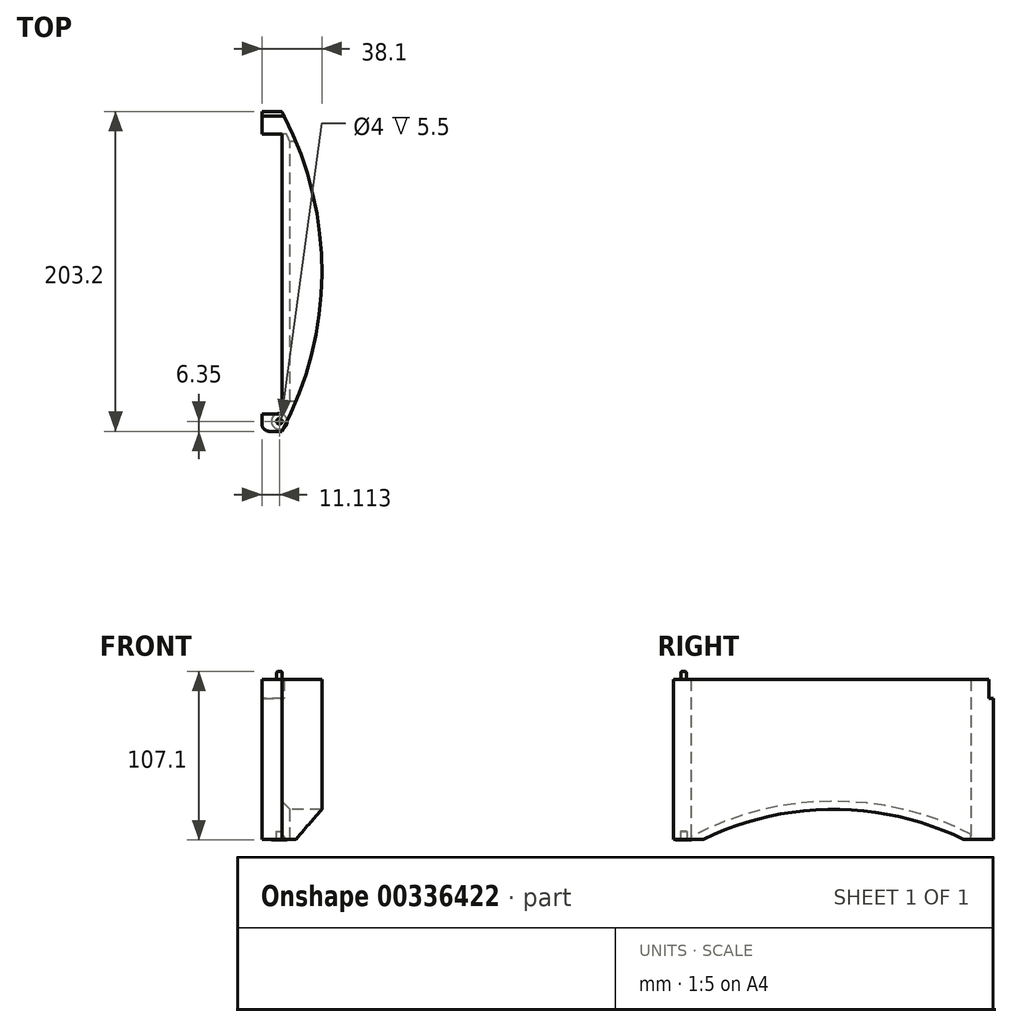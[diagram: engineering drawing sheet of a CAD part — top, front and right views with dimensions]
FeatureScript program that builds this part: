
annotation { "Feature Type Name" : "Feature", "Feature Type Description" : "" }
export const myFeature = defineFeature(function(context is Context, id is Id, definition is map)
    precondition{}
    {
        {
            var Q0;
            Q0=qCreatedBy(makeId("Right.planeOp"),FACE);
            var sketch = newSketch(context, id + "F0", { "sketchPlane" : qUnion([Q0])});
            skLineSegment(sketch, "E0", {"start": v(0, 0) * mm, "end": v(52.75, 0) * mm});
            skLineSegment(sketch, "E1", {"start": v(101.6, 0) * mm, "end": v(101.6, 166.73) * mm, "construction": true});
            skPoint(sketch, "E1.startSnap0", {"position": v(101.6, 30.6) * mm});
            skLineSegment(sketch, "E2", {"start": v(0, 0) * mm, "end": v(0, 101.6) * mm});
            skLineSegment(sketch, "E3", {"start": v(0, 101.6) * mm, "end": v(101.6, 101.6) * mm});
            skLineSegment(sketch, "E4", {"start": v(52.75, 0) * mm, "end": v(101.6, 0) * mm});
            skLineSegment(sketch, "E5.MirrorCS", {"start": v(203.2, 0) * mm, "end": v(203.2, 101.6) * mm});
            skLineSegment(sketch, "E6.MirrorCS", {"start": v(150.45, 0) * mm, "end": v(101.6, 0) * mm});
            skLineSegment(sketch, "E7.MirrorCS", {"start": v(203.2, 101.6) * mm, "end": v(101.6, 101.6) * mm});
            skLineSegment(sketch, "E8.MirrorCS", {"start": v(203.2, 0) * mm, "end": v(150.45, 0) * mm});
            skSolve(sketch);
        }
        {
            var Q0;
            Q0 = qSketchRegion(id + "F0", true);
            extrude(context, id + "F1", {"entities" : qUnion([Q0]), "depth" : 12.7 * mm});
        }
        {
            var Q0;
            Q0=makeQuery(id+"F1.opExtrude","SWEPT_FACE",FACE,{"disambiguationData":[OSD([sQuery(id+"F0.wireOp",EDGE,"E0"),sQuery(id+"F0.wireOp",EDGE,"E4"),sQuery(id+"F0.wireOp",EDGE,"E6.MirrorCS"),sQuery(id+"F0.wireOp",EDGE,"E8.MirrorCS")])]});
            var sketch = newSketch(context, id + "F2", { "sketchPlane" : qUnion([Q0])});
            skArc(sketch, "E9", {"start": v(12.7, -203.2) * mm, "mid": v(38.1, -101.6) * mm, "end": v(12.7, 0) * mm});
            skLineSegment(sketch, "E10", {"start": v(12.7, 0) * mm, "end": v(12.7, -203.2) * mm});
            skSolve(sketch);
        }
        {
            var Q0;
            Q0 = qSketchRegion(id + "F2", true);
            var Q1;
            Q1=makeQuery(id+"F1.opExtrude","SWEPT_FACE",FACE,{"disambiguationData":[OSD([sQuery(id+"F0.wireOp",EDGE,"E3"),sQuery(id+"F0.wireOp",EDGE,"E7.MirrorCS")])]});
            extrude(context, id + "F3", {"entities" : qUnion([Q0]), "operationType" : NewBodyOperationType.ADD, "endBound" : BoundingType.UP_TO_SURFACE, "oppositeDirection" : true, "endBoundEntityFace" : qUnion([Q1]), "depth" : 25 * mm});
        }
        {
            var Q0;
            Q0=makeQuery(id+"F1.opExtrude","CAP_FACE",FACE,{"disambiguationData":[OSD([sQuery(id+"F0.wireOp",EDGE,"E0"),sQuery(id+"F0.wireOp",EDGE,"E2"),sQuery(id+"F0.wireOp",EDGE,"E3"),sQuery(id+"F0.wireOp",EDGE,"E4"),sQuery(id+"F0.wireOp",EDGE,"E5.MirrorCS"),sQuery(id+"F0.wireOp",EDGE,"E6.MirrorCS"),sQuery(id+"F0.wireOp",EDGE,"E7.MirrorCS"),sQuery(id+"F0.wireOp",EDGE,"E8.MirrorCS")])],"isStart":true});
            var sketch = newSketch(context, id + "F4", { "sketchPlane" : qUnion([Q0])});
            skArc(sketch, "E11", {"start": v(-19.05, 0) * mm, "mid": v(-101.6, 19.05) * mm, "end": v(-184.15, 0) * mm});
            skLineSegment(sketch, "E12", {"start": v(-184.15, 0) * mm, "end": v(-19.05, 0) * mm});
            skLineSegment(sketch, "E13", {"start": v(-101.6, 0) * mm, "end": v(-101.6, 101.6) * mm});
            skSolve(sketch);
        }
        {
            var Q0;
            Q0 = qSketchRegion(id + "F4", true);
            extrude(context, id + "F5", {"entities" : qUnion([Q0]), "operationType" : NewBodyOperationType.REMOVE, "endBound" : BoundingType.THROUGH_ALL, "oppositeDirection" : true, "depth" : 25 * mm});
        }
        {
            var Q0;
            Q0=makeQuery(id+"F1.opExtrude","CAP_FACE",FACE,{"disambiguationData":[OSD([sQuery(id+"F0.wireOp",EDGE,"E0"),sQuery(id+"F0.wireOp",EDGE,"E2"),sQuery(id+"F0.wireOp",EDGE,"E3"),sQuery(id+"F0.wireOp",EDGE,"E4"),sQuery(id+"F0.wireOp",EDGE,"E5.MirrorCS"),sQuery(id+"F0.wireOp",EDGE,"E6.MirrorCS"),sQuery(id+"F0.wireOp",EDGE,"E7.MirrorCS"),sQuery(id+"F0.wireOp",EDGE,"E8.MirrorCS")])],"isStart":true});
            var sketch = newSketch(context, id + "F6", { "sketchPlane" : qUnion([Q0])});
            skLineSegment(sketch, "E14.bottom", {"start": v(-242.75, 138.92) * mm, "end": v(-200.2, 138.92) * mm});
            skLineSegment(sketch, "E14.top", {"start": v(-242.75, 89.43) * mm, "end": v(-200.2, 89.43) * mm});
            skLineSegment(sketch, "E14.left", {"start": v(-242.75, 138.92) * mm, "end": v(-242.75, 89.43) * mm});
            skLineSegment(sketch, "E14.right", {"start": v(-200.2, 138.92) * mm, "end": v(-200.2, 89.43) * mm});
            skSolve(sketch);
        }
        {
            var Q0;
            Q0 = qSketchRegion(id + "F6", true);
            extrude(context, id + "F7", {"entities" : qUnion([Q0]), "operationType" : NewBodyOperationType.REMOVE, "endBound" : BoundingType.THROUGH_ALL, "oppositeDirection" : true, "depth" : 25 * mm});
        }
        {
            var Q0;
            {var subQ0=sQuery(id+"F0.wireOp",EDGE,"E8.MirrorCS");var subQ1=sQuery(id+"F0.wireOp",EDGE,"E6.MirrorCS");var subQ2=sQuery(id+"F0.wireOp",EDGE,"E4");var subQ3=sQuery(id+"F0.wireOp",EDGE,"E2");var subQ4=sQuery(id+"F0.wireOp",EDGE,"E0");var subQ5=sQuery(id+"F2.wireOp",EDGE,"E9");Q0=makeQuery(id+"F5.boolean.opBoolean","SPLIT",FACE,{"disambiguationData":[TD([makeQuery(id+"F1.opExtrude","SWEPT_FACE",FACE,{"disambiguationData":[OSD([subQ3])]})])],"derivedFrom":makeQuery(id+"F3.boolean.opBoolean","MERGE",FACE,{"derivedFrom":[makeQuery(id+"F1.opExtrude","SWEPT_FACE",FACE,{"disambiguationData":[OSD([subQ4,subQ2,subQ1,subQ0])]}),makeQuery(id+"F3.opExtrude","CAP_FACE",FACE,{"disambiguationData":[OSD([subQ5,sQuery(id+"F2.wireOp",EDGE,"E10")])],"isStart":true})]})});}
            var sketch = newSketch(context, id + "F8", { "sketchPlane" : qUnion([Q0])});
            skCircle(sketch, "E15", {"center": v(11.11, -6.35) * mm, "radius": 2 * mm});
            skSolve(sketch);
        }
        {
            var Q0;
            Q0 = qSketchRegion(id + "F8", true);
            extrude(context, id + "F9", {"entities" : qUnion([Q0]), "operationType" : NewBodyOperationType.REMOVE, "oppositeDirection" : true, "depth" : 5 * mm});
        }
        {
            var Q0;
            {var subQ0=sQuery(id+"F0.wireOp",EDGE,"E8.MirrorCS");var subQ1=sQuery(id+"F0.wireOp",EDGE,"E6.MirrorCS");var subQ2=sQuery(id+"F0.wireOp",EDGE,"E4");var subQ3=sQuery(id+"F0.wireOp",EDGE,"E2");var subQ4=sQuery(id+"F0.wireOp",EDGE,"E0");var subQ5=sQuery(id+"F2.wireOp",EDGE,"E9");Q0=makeQuery(id+"F5.boolean.opBoolean","SPLIT",FACE,{"disambiguationData":[TD([makeQuery(id+"F1.opExtrude","SWEPT_FACE",FACE,{"disambiguationData":[OSD([subQ3])]})])],"derivedFrom":makeQuery(id+"F3.boolean.opBoolean","MERGE",FACE,{"derivedFrom":[makeQuery(id+"F1.opExtrude","SWEPT_FACE",FACE,{"disambiguationData":[OSD([subQ4,subQ2,subQ1,subQ0])]}),makeQuery(id+"F3.opExtrude","CAP_FACE",FACE,{"disambiguationData":[OSD([subQ5,sQuery(id+"F2.wireOp",EDGE,"E10")])],"isStart":true})]})});}
            var sketch = newSketch(context, id + "F10", { "sketchPlane" : qUnion([Q0])});
            skCircle(sketch, "E16", {"center": v(11.11, -6.35) * mm, "radius": 5 * mm});
            skCircle(sketch, "E17.0", {"center": v(11.11, -6.35) * mm, "radius": 2 * mm});
            skSolve(sketch);
        }
        {
            var Q0;
            Q0 = qSketchRegion(id + "F10", true);
            extrude(context, id + "F11", {"entities" : qUnion([Q0]), "operationType" : NewBodyOperationType.ADD, "depth" : .5 * mm});
        }
        {
            var Q0;
            {var subQ0=sQuery(id+"F0.wireOp",EDGE,"E7.MirrorCS");var subQ1=sQuery(id+"F0.wireOp",EDGE,"E3");Q0=makeQuery(id+"F3.boolean.opBoolean","MERGE",FACE,{"derivedFrom":[makeQuery(id+"F1.opExtrude","SWEPT_FACE",FACE,{"disambiguationData":[OSD([subQ1,subQ0])]}),makeQuery(id+"F3.opExtrude","CAP_FACE",FACE,{"disambiguationData":[OSD([subQ1,subQ0])],"isStart":false})]});}
            var sketch = newSketch(context, id + "F12", { "sketchPlane" : qUnion([Q0])});
            skCircle(sketch, "E18.0", {"center": v(11.11, 6.35) * mm, "radius": 2 * mm, "construction": true});
            skCircle(sketch, "E19.0", {"center": v(11.11, 6.35) * mm, "radius": 1.8 * mm});
            skSolve(sketch);
        }
        {
            var Q0;
            Q0 = qSketchRegion(id + "F12", true);
            extrude(context, id + "F13", {"entities" : qUnion([Q0]), "operationType" : NewBodyOperationType.ADD, "depth" : 5 * mm});
        }
        {
            var Q0;
            Q0=makeQuery(id+"F13.opExtrude","CAP_EDGE",EDGE,{"disambiguationData":[OSD([sQuery(id+"F12.wireOp",EDGE,"E19.0")])],"isStart":false});
            fillet(context, id + "F14", {"entities" : qUnion([Q0]), "radius" : 1 * mm, "tangentPropagation" : true, "allowEdgeOverflow" : false});
        }
        {
            var Q0;
            Q0=makeQuery(id+"F1.opExtrude","CAP_FACE",FACE,{"disambiguationData":[OSD([sQuery(id+"F0.wireOp",EDGE,"E0"),sQuery(id+"F0.wireOp",EDGE,"E2"),sQuery(id+"F0.wireOp",EDGE,"E3"),sQuery(id+"F0.wireOp",EDGE,"E4"),sQuery(id+"F0.wireOp",EDGE,"E5.MirrorCS"),sQuery(id+"F0.wireOp",EDGE,"E6.MirrorCS"),sQuery(id+"F0.wireOp",EDGE,"E7.MirrorCS"),sQuery(id+"F0.wireOp",EDGE,"E8.MirrorCS")])],"isStart":true});
            var sketch = newSketch(context, id + "F15", { "sketchPlane" : qUnion([Q0])});
            skLineSegment(sketch, "E20", {"start": v(-100.1, 101.6) * mm, "end": v(-100.1, 0) * mm, "construction": true});
            skLineSegment(sketch, "E21", {"start": v(-189, 101.6) * mm, "end": v(-189, 0) * mm});
            skLineSegment(sketch, "E22", {"start": v(-189, 0) * mm, "end": v(-100.1, 0) * mm});
            skLineSegment(sketch, "E23", {"start": v(-189, 101.6) * mm, "end": v(-100.1, 101.6) * mm});
            skLineSegment(sketch, "E24.MirrorCS", {"start": v(-11.2, 101.6) * mm, "end": v(-100.1, 101.6) * mm});
            skLineSegment(sketch, "E25.MirrorCS", {"start": v(-11.2, 101.6) * mm, "end": v(-11.2, 0) * mm});
            skLineSegment(sketch, "E26.MirrorCS", {"start": v(-11.2, 0) * mm, "end": v(-100.1, 0) * mm});
            skSolve(sketch);
        }
        {
            var Q0;
            Q0 = qSketchRegion(id + "F15", true);
            extrude(context, id + "F16", {"entities" : qUnion([Q0]), "operationType" : NewBodyOperationType.REMOVE, "oppositeDirection" : true, "depth" : 12.7 * mm});
        }
        {
            var Q0;
            Q0=makeQuery(id+"F1.opExtrude","CAP_EDGE",EDGE,{"disambiguationData":[OSD([sQuery(id+"F0.wireOp",EDGE,"E2")])],"isStart":true});
            var Q1;
            Q1=makeQuery(id+"F16.boolean.opBoolean","COPY",EDGE,{"derivedFrom":makeQuery(id+"F16.opExtrude","CAP_EDGE",EDGE,{"disambiguationData":[OSD([sQuery(id+"F15.wireOp",EDGE,"E25.MirrorCS")])],"isStart":true})});
            fillet(context, id + "F17", {"entities" : qUnion([Q0, Q1]), "radius" : 5.08 * mm, "tangentPropagation" : true, "allowEdgeOverflow" : false});
        }
        {
            var Q0;
            Q0=makeQuery(id+"F16.boolean.opBoolean","INTERSECT",EDGE,{"derivedFrom":[makeQuery(id+"F5.boolean.opBoolean","COPY",FACE,{"derivedFrom":makeQuery(id+"F5.opExtrude","SWEPT_FACE",FACE,{"disambiguationData":[OSD([sQuery(id+"F4.wireOp",EDGE,"E11")])]})}),makeQuery(id+"F16.opExtrude","CAP_FACE",FACE,{"disambiguationData":[OSD([sQuery(id+"F15.wireOp",EDGE,"E21"),sQuery(id+"F15.wireOp",EDGE,"E22"),sQuery(id+"F15.wireOp",EDGE,"E23"),sQuery(id+"F15.wireOp",EDGE,"E24.MirrorCS"),sQuery(id+"F15.wireOp",EDGE,"E25.MirrorCS"),sQuery(id+"F15.wireOp",EDGE,"E26.MirrorCS")])],"isStart":false})]});
            chamfer(context, id + "F18", {"entities" : qUnion([Q0]), "width" : 5.08 * mm, "tangentPropagation" : true});
        }
    });
